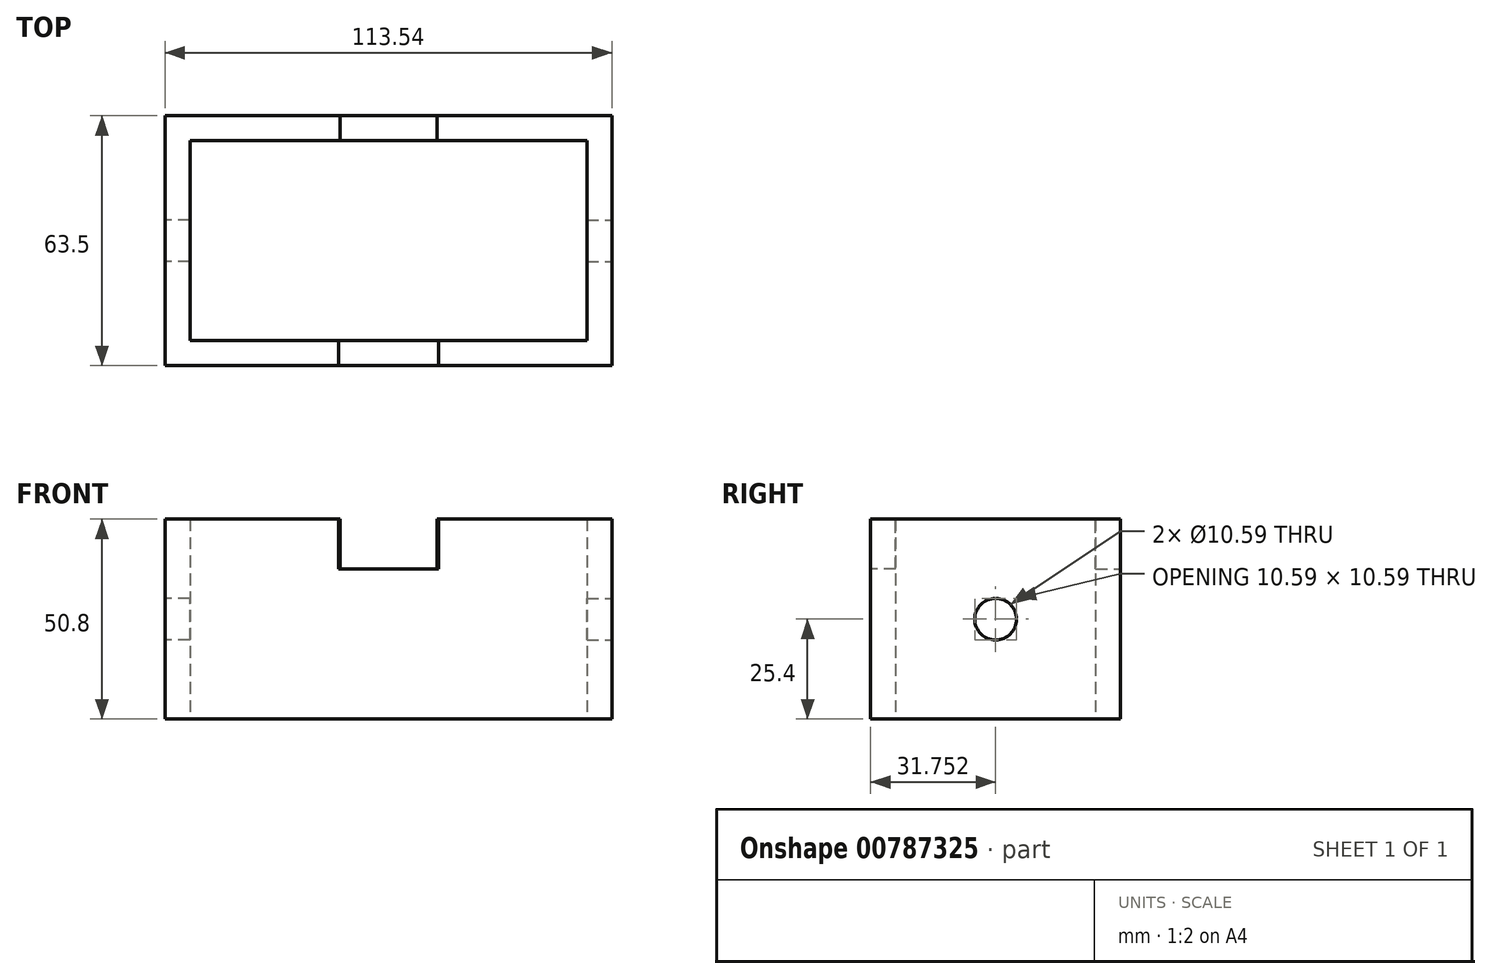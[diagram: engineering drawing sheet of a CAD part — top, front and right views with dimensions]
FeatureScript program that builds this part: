
annotation { "Feature Type Name" : "Feature", "Feature Type Description" : "" }
export const myFeature = defineFeature(function(context is Context, id is Id, definition is map)
    precondition{}
    {
        {
            var Q0;
            Q0=qCreatedBy(makeId("Top.planeOp"),FACE);
            var sketch = newSketch(context, id + "F0", { "sketchPlane" : qUnion([Q0])});
            skLineSegment(sketch, "E0", {"start": v(-50.42, 40.74) * mm, "end": v(-50.42, -10.06) * mm});
            skLineSegment(sketch, "E1", {"start": v(-50.42, -10.06) * mm, "end": v(0, -10.06) * mm});
            skLineSegment(sketch, "E2", {"start": v(0.38, 40.74) * mm, "end": v(-50.42, 40.74) * mm});
            skLineSegment(sketch, "E3", {"start": v(0, -10.06) * mm, "end": v(0, -16.4) * mm});
            skLineSegment(sketch, "E4", {"start": v(0.38, 40.74) * mm, "end": v(0.38, 47.1) * mm});
            skLineSegment(sketch, "E5", {"start": v(0, -16.4) * mm, "end": v(-56.77, -16.4) * mm});
            skLineSegment(sketch, "E6", {"start": v(-56.77, -16.4) * mm, "end": v(-56.77, 15.34) * mm});
            skLineSegment(sketch, "E7", {"start": v(-56.77, 15.34) * mm, "end": v(-56.77, 47.1) * mm});
            skLineSegment(sketch, "E8", {"start": v(-56.77, 47.1) * mm, "end": v(0.38, 47.1) * mm});
            skLineSegment(sketch, "E9", {"start": v(0, -10.06) * mm, "end": v(0.38, 40.74) * mm});
            skSolve(sketch);
        }
        {
            var Q0;
            Q0=makeQuery(id+"F0.imprint","IMPRINT",FACE,{"disambiguationData":[TD([[makeQuery(id+"F0.imprint","IMPRINT",EDGE,{"derivedFrom":sQuery(id+"F0.wireOp",EDGE,"E0")}),-1.0]])]});
            extrude(context, id + "F1", {"entities" : qUnion([Q0]), "depth" : 50.8 * mm, "offsetDistance" : 25.4 * mm});
        }
        {
            var Q0;
            Q0=makeQuery(id+"F1.opExtrude","SWEPT_FACE",FACE,{"disambiguationData":[OSD([sQuery(id+"F0.wireOp",EDGE,"E5")])]});
            var sketch = newSketch(context, id + "F2", { "sketchPlane" : qUnion([Q0])});
            skLineSegment(sketch, "E10", {"start": v(-12.7, 50.8) * mm, "end": v(-12.7, 38.1) * mm});
            skLineSegment(sketch, "E11", {"start": v(-12.7, 38.1) * mm, "end": v(0, 38.1) * mm});
            skSolve(sketch);
        }
        {
            var Q0;
            Q0=makeQuery(id+"F1.opExtrude","SWEPT_FACE",FACE,{"disambiguationData":[OSD([sQuery(id+"F0.wireOp",EDGE,"E8")])]});
            var sketch = newSketch(context, id + "F3", { "sketchPlane" : qUnion([Q0])});
            skLineSegment(sketch, "E12", {"start": v(12.32, 50.8) * mm, "end": v(12.32, 38.1) * mm});
            skLineSegment(sketch, "E13", {"start": v(12.32, 38.1) * mm, "end": v(-0.38, 38.1) * mm});
            skSolve(sketch);
        }
        {
            var Q0;
            {var subQ0=sQuery(id+"F2.wireOp",EDGE,"E10");Q0=makeQuery(id+"F2.imprint","IMPRINT",FACE,{"disambiguationData":[TD([[makeQuery(id+"F2.imprint","IMPRINT",EDGE,{"derivedFrom":subQ0}),1.0]])]});}
            extrude(context, id + "F4", {"entities" : qUnion([Q0]), "operationType" : NewBodyOperationType.REMOVE, "oppositeDirection" : true, "depth" : 25.4 * mm, "offsetDistance" : 25.4 * mm});
        }
        {
            var Q0;
            {var subQ0=sQuery(id+"F3.wireOp",EDGE,"E12");Q0=makeQuery(id+"F3.imprint","IMPRINT",FACE,{"disambiguationData":[TD([[makeQuery(id+"F3.imprint","IMPRINT",EDGE,{"derivedFrom":subQ0}),-1.0]])]});}
            extrude(context, id + "F5", {"entities" : qUnion([Q0]), "operationType" : NewBodyOperationType.REMOVE, "oppositeDirection" : true, "depth" : 25.4 * mm, "offsetDistance" : 25.4 * mm});
        }
        {
            var Q0;
            Q0=makeQuery(id+"F1.opExtrude","SWEPT_FACE",FACE,{"disambiguationData":[OSD([sQuery(id+"F0.wireOp",EDGE,"E6"),sQuery(id+"F0.wireOp",EDGE,"E7")])]});
            var sketch = newSketch(context, id + "F6", { "sketchPlane" : qUnion([Q0])});
            skCircle(sketch, "E14", {"center": v(-15.34, 25.4) * mm, "radius": 5.3 * mm});
            skPoint(sketch, "E15.trimOffspring.end.orphan", {"position": v(-15.34, 0) * mm});
            skSolve(sketch);
        }
        {
            var Q0;
            Q0=makeQuery(id+"F6.imprint","IMPRINT",FACE,{"disambiguationData":[TD([[makeQuery(id+"F6.imprint","IMPRINT",EDGE,{"derivedFrom":sQuery(id+"F6.wireOp",EDGE,"E14")}),1.0]])]});
            extrude(context, id + "F7", {"entities" : qUnion([Q0]), "operationType" : NewBodyOperationType.REMOVE, "oppositeDirection" : true, "depth" : 25.4 * mm, "offsetDistance" : 25.4 * mm});
        }
        {
            var Q0;
            Q0=makeQuery(id+"F1.opExtrude","SWEPT_BODY",BODY,{"disambiguationData":[OSD([sQuery(id+"F0.wireOp",EDGE,"E0"),sQuery(id+"F0.wireOp",EDGE,"E1"),sQuery(id+"F0.wireOp",EDGE,"E2"),sQuery(id+"F0.wireOp",EDGE,"E3"),sQuery(id+"F0.wireOp",EDGE,"E4"),sQuery(id+"F0.wireOp",EDGE,"E5"),sQuery(id+"F0.wireOp",EDGE,"E6"),sQuery(id+"F0.wireOp",EDGE,"E7"),sQuery(id+"F0.wireOp",EDGE,"E8")])]});
            var Q1;
            Q1=makeQuery(id+"F1.opExtrude","SWEPT_FACE",FACE,{"disambiguationData":[OSD([sQuery(id+"F0.wireOp",EDGE,"E3")])]});
            mirror(context, id + "F8", {"operationType" : NewBodyOperationType.ADD, "entities" : qUnion([Q0]), "mirrorPlane" : qUnion([Q1])});
        }
    });
